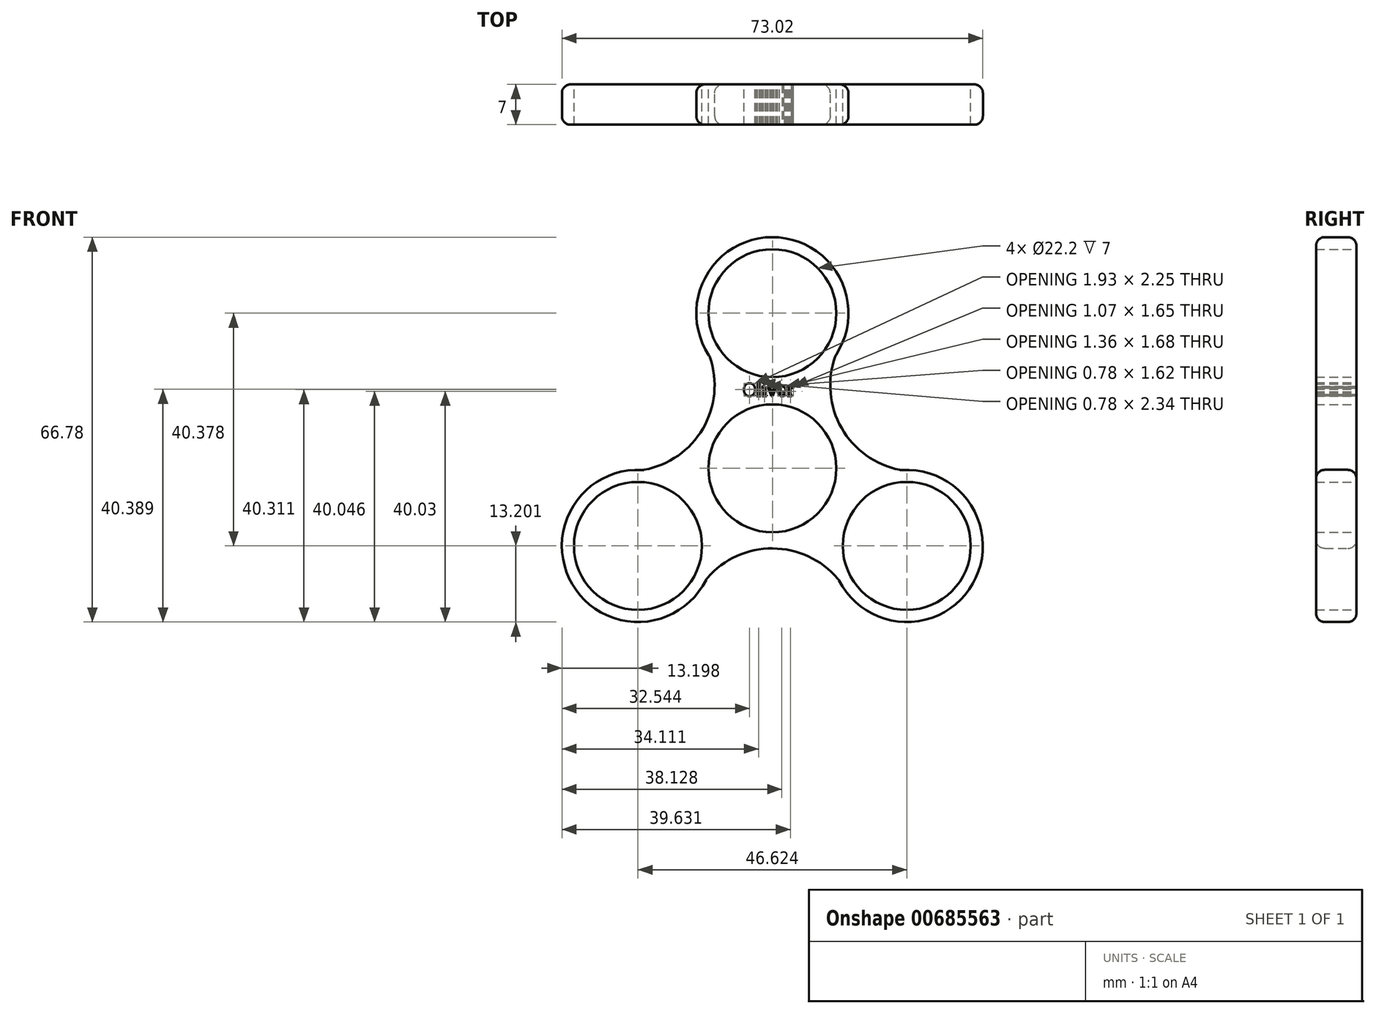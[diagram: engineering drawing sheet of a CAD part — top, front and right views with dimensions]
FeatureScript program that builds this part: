
annotation { "Feature Type Name" : "Feature", "Feature Type Description" : "" }
export const myFeature = defineFeature(function(context is Context, id is Id, definition is map)
    precondition{}
    {
        {
            var Q0;
            Q0=qCreatedBy(makeId("Front.planeOp"),FACE);
            var sketch = newSketch(context, id + "F0", { "sketchPlane" : qUnion([Q0])});
            skCircle(sketch, "E0", {"center": v(0, 0) * mm, "radius": 11.1 * mm});
            skCircle(sketch, "E1", {"center": v(0, 26.92) * mm, "radius": 11.1 * mm});
            skArc(sketch, "E2", {"start": v(10.96, 19.56) * mm, "mid": v(-0.06, 40.12) * mm, "end": v(-10.89, 19.46) * mm});
            skArc(sketch, "E3.1.0", {"start": v(-22.42, -0.29) * mm, "mid": v(-34.71, -20.11) * mm, "end": v(-11.4, -19.16) * mm});
            skArc(sketch, "E3.2.0", {"start": v(11.46, -19.27) * mm, "mid": v(34.77, -20) * mm, "end": v(22.3, -0.3) * mm});
            skCircle(sketch, "E4", {"center": v(-23.31, -13.46) * mm, "radius": 11.1 * mm});
            skCircle(sketch, "E5", {"center": v(23.31, -13.46) * mm, "radius": 11.1 * mm});
            skArc(sketch, "E6", {"start": v(-22.42, -0.29) * mm, "mid": v(-12.06, 6.9) * mm, "end": v(-10.89, 19.46) * mm});
            skArc(sketch, "E7.1.0", {"start": v(11.46, -19.27) * mm, "mid": v(0.05, -13.9) * mm, "end": v(-11.4, -19.16) * mm});
            skArc(sketch, "E7.2.0", {"start": v(10.96, 19.56) * mm, "mid": v(12, 7) * mm, "end": v(22.3, -0.3) * mm});
            skText(sketch, "E8", { "text": "Oliver", "fontName": "RobotoSlab-Regular.ttf"});
            const initialGuessF0  = {"E8": [-0.00505, 0.01256, 1, 0, 0.00221]};
            skSetInitialGuess(sketch, initialGuessF0);
            skSolve(sketch);
        }
        {
            var Q0;
            Q0=makeQuery(id+"F0.imprint","IMPRINT",FACE,{"disambiguationData":[TD([[makeQuery(id+"F0.imprint","IMPRINT",EDGE,{"derivedFrom":sQuery(id+"F0.wireOp",EDGE,"E0")}),-1.0]])]});
            extrude(context, id + "F1", {"entities" : qUnion([Q0]), "depth" : 7 * mm, "offsetDistance" : 25 * mm});
        }
        {
            var Q0;
            Q0=makeQuery(id+"F1.opExtrude","SWEPT_FACE",FACE,{"disambiguationData":[OSD([sQuery(id+"F0.wireOp",EDGE,"E3.1.0")])]});
            var Q1;
            Q1=makeQuery(id+"F1.opExtrude","SWEPT_FACE",FACE,{"disambiguationData":[OSD([sQuery(id+"F0.wireOp",EDGE,"E7.1.0")])]});
            var Q2;
            Q2=makeQuery(id+"F1.opExtrude","SWEPT_FACE",FACE,{"disambiguationData":[OSD([sQuery(id+"F0.wireOp",EDGE,"E3.2.0")])]});
            var Q3;
            Q3=makeQuery(id+"F1.opExtrude","SWEPT_FACE",FACE,{"disambiguationData":[OSD([sQuery(id+"F0.wireOp",EDGE,"E7.2.0")])]});
            var Q4;
            Q4=makeQuery(id+"F1.opExtrude","SWEPT_FACE",FACE,{"disambiguationData":[OSD([sQuery(id+"F0.wireOp",EDGE,"E2")])]});
            var Q5;
            Q5=makeQuery(id+"F1.opExtrude","SWEPT_FACE",FACE,{"disambiguationData":[OSD([sQuery(id+"F0.wireOp",EDGE,"E6")])]});
            fillet(context, id + "F2", {"entities" : qUnion([Q0, Q1, Q2, Q3, Q4, Q5]), "radius" : 1.5 * mm, "tangentPropagation" : true, "allowEdgeOverflow" : false});
        }
    });
